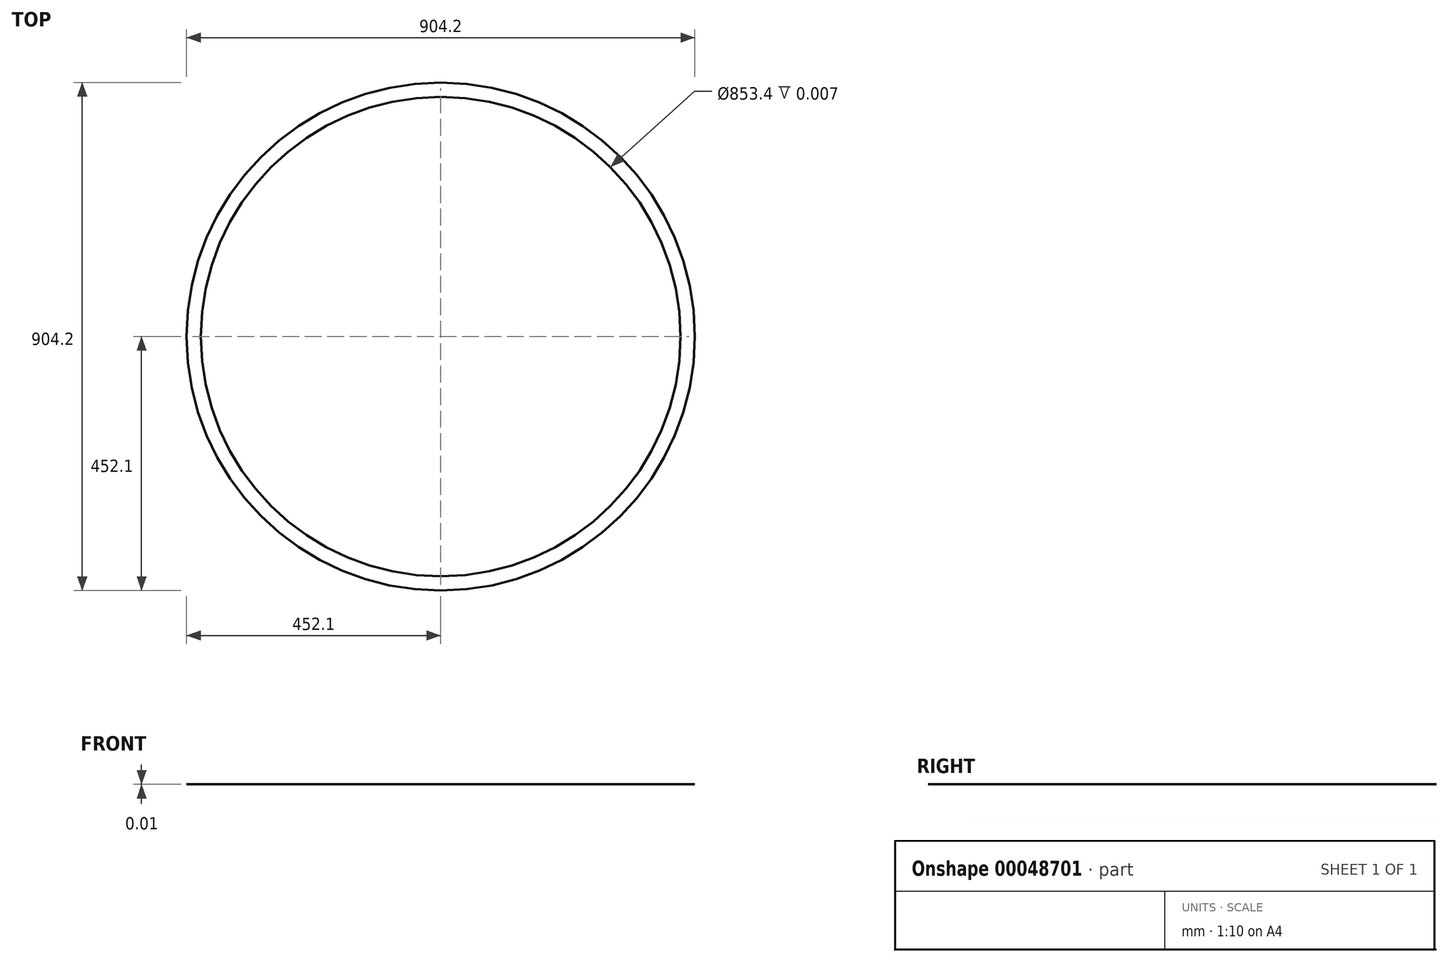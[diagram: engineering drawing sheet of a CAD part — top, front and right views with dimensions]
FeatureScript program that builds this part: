
annotation { "Feature Type Name" : "Feature", "Feature Type Description" : "" }
export const myFeature = defineFeature(function(context is Context, id is Id, definition is map)
    precondition{}
    {
        {
            var Q0;
            Q0=qCreatedBy(makeId("Top.planeOp"),FACE);
            var sketch = newSketch(context, id + "F0", { "sketchPlane" : qUnion([Q0])});
            skCircle(sketch, "E0", {"center": v(0, 0) * mm, "radius": 452.1 * mm});
            skCircle(sketch, "E1", {"center": v(0, 0) * mm, "radius": 426.7 * mm});
            skSolve(sketch);
        }
        {
            var Q0;
            Q0 = qSketchRegion(id + "F0", true);
            extrude(context, id + "F1", {"entities" : qUnion([Q0]), "depth" : 3 / 457.2 * mm});
        }
    });
